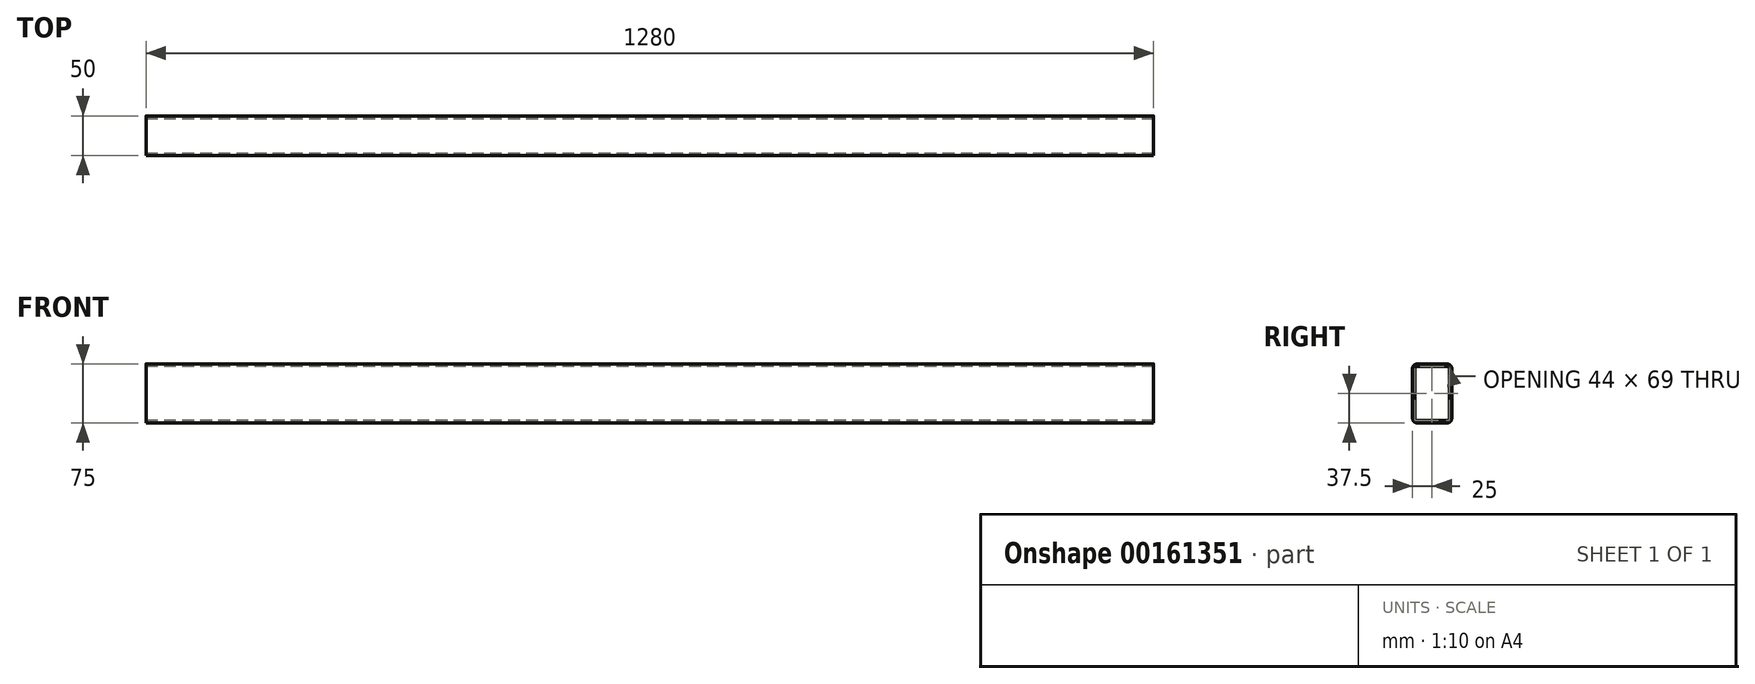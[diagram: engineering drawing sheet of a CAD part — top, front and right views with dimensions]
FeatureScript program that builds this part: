
annotation { "Feature Type Name" : "Feature", "Feature Type Description" : "" }
export const myFeature = defineFeature(function(context is Context, id is Id, definition is map)
    precondition{}
    {
        {
            var Q0;
            Q0=qCreatedBy(makeId("Right.planeOp"),FACE);
            var sketch = newSketch(context, id + "F0", { "sketchPlane" : qUnion([Q0])});
            skLineSegment(sketch, "E0.bottom", {"start": v(25, 37.5) * mm, "end": v(-25, 37.5) * mm});
            skLineSegment(sketch, "E0.top", {"start": v(25, -37.5) * mm, "end": v(-25, -37.5) * mm});
            skLineSegment(sketch, "E0.left", {"start": v(25, 37.5) * mm, "end": v(25, -37.5) * mm});
            skLineSegment(sketch, "E0.right", {"start": v(-25, 37.5) * mm, "end": v(-25, -37.5) * mm});
            skPoint(sketch, "E0.middle", {"position": v(0, 0) * mm});
            skSolve(sketch);
        }
        {
            var Q0;
            Q0=makeQuery(id+"F0.imprint","IMPRINT",FACE,{"disambiguationData":[TD([[makeQuery(id+"F0.imprint","IMPRINT",EDGE,{"derivedFrom":sQuery(id+"F0.wireOp",EDGE,"E0.bottom")}),1.0]])]});
            extrude(context, id + "F1", {"entities" : qUnion([Q0]), "flatOperationType" : FlatOperationType.REMOVE, "offsetDistance" : 25 * mm, "depth" : 1280 * mm, "domain" : OperationDomain.MODEL});
        }
        {
            var Q0;
            Q0=makeQuery(id+"F1.opExtrude","SWEPT_EDGE",EDGE,{"disambiguationData":[OSD([sQuery(id+"F0.wireOp",EDGE,"E0.bottom"),sQuery(id+"F0.wireOp",EDGE,"E0.left")])]});
            var Q1;
            Q1=makeQuery(id+"F1.opExtrude","SWEPT_EDGE",EDGE,{"disambiguationData":[OSD([sQuery(id+"F0.wireOp",EDGE,"E0.bottom"),sQuery(id+"F0.wireOp",EDGE,"E0.right")])]});
            var Q2;
            Q2=makeQuery(id+"F1.opExtrude","SWEPT_EDGE",EDGE,{"disambiguationData":[OSD([sQuery(id+"F0.wireOp",EDGE,"E0.top"),sQuery(id+"F0.wireOp",EDGE,"E0.left")])]});
            var Q3;
            Q3=makeQuery(id+"F1.opExtrude","SWEPT_EDGE",EDGE,{"disambiguationData":[OSD([sQuery(id+"F0.wireOp",EDGE,"E0.top"),sQuery(id+"F0.wireOp",EDGE,"E0.right")])]});
            fillet(context, id + "F2", {"entities" : qUnion([Q0, Q1, Q2, Q3]), "radius" : 6 * mm, "tangentPropagation" : true, "allowEdgeOverflow" : false});
        }
        {
            var Q0;
            Q0=makeQuery(id+"F1.opExtrude","CAP_FACE",FACE,{"disambiguationData":[OSD([sQuery(id+"F0.wireOp",EDGE,"E0.bottom"),sQuery(id+"F0.wireOp",EDGE,"E0.top"),sQuery(id+"F0.wireOp",EDGE,"E0.left"),sQuery(id+"F0.wireOp",EDGE,"E0.right")])],"isStart":true});
            var Q1;
            Q1=makeQuery(id+"F1.opExtrude","CAP_FACE",FACE,{"disambiguationData":[OSD([sQuery(id+"F0.wireOp",EDGE,"E0.bottom"),sQuery(id+"F0.wireOp",EDGE,"E0.top"),sQuery(id+"F0.wireOp",EDGE,"E0.left"),sQuery(id+"F0.wireOp",EDGE,"E0.right")])],"isStart":false});
            shell(context, id + "F3", {"entities" : qUnion([Q0, Q1]), "thickness" : 3 * mm});
        }
    });
